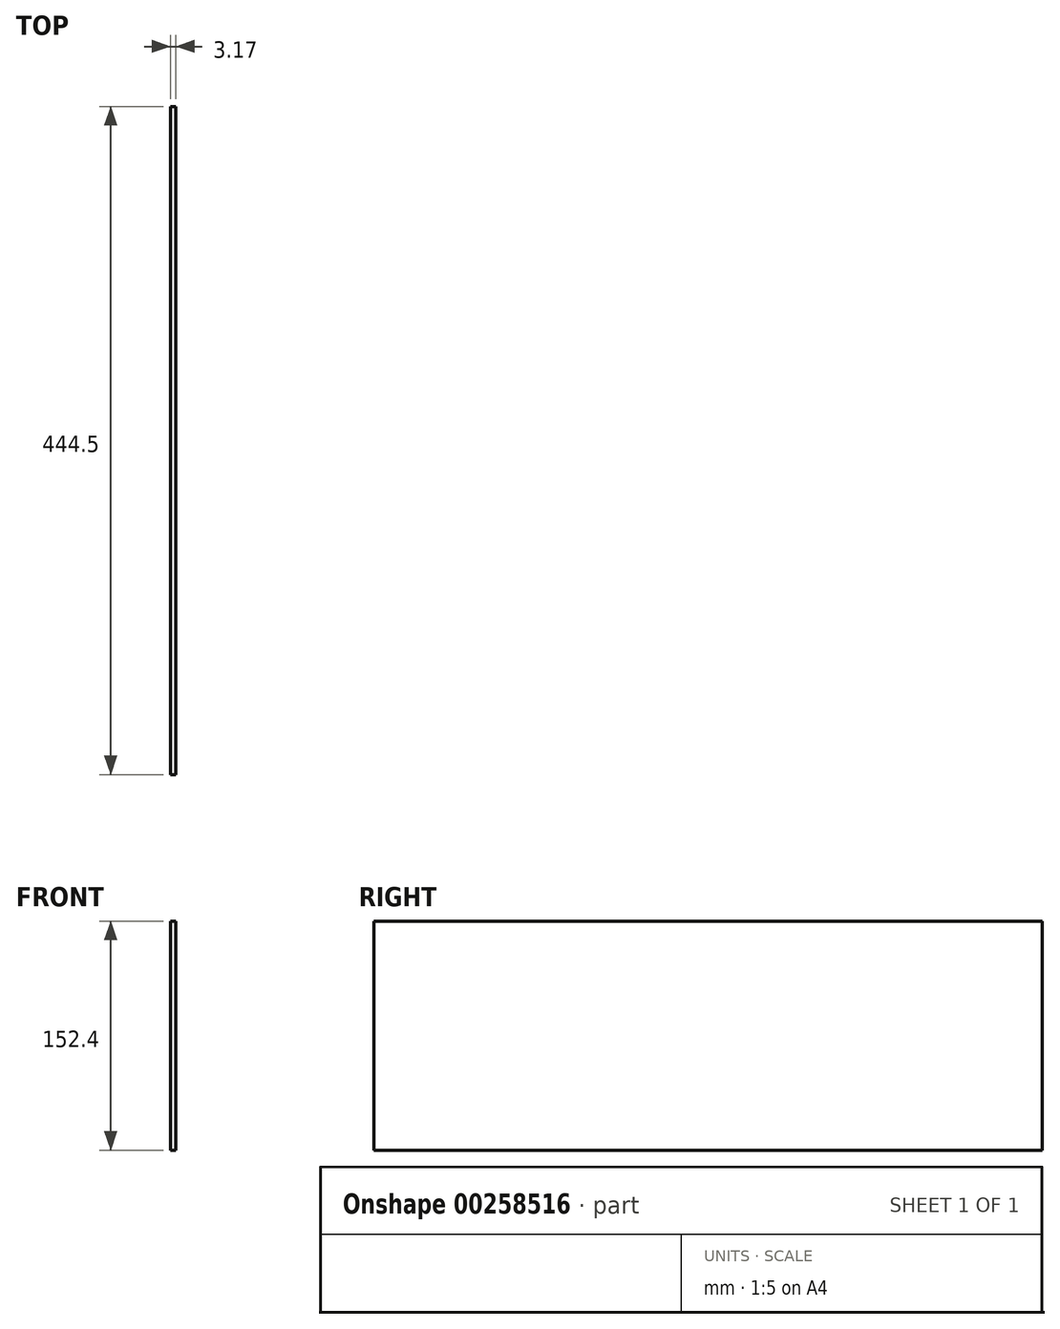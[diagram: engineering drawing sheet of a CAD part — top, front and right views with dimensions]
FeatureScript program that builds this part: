
annotation { "Feature Type Name" : "Feature", "Feature Type Description" : "" }
export const myFeature = defineFeature(function(context is Context, id is Id, definition is map)
    precondition{}
    {
        {
            var Q0;
            Q0=qCreatedBy(makeId("Right.planeOp"),FACE);
            var sketch = newSketch(context, id + "F0", { "sketchPlane" : qUnion([Q0])});
            skLineSegment(sketch, "E0.bottom", {"start": v(222.25, 76.2) * mm, "end": v(-222.25, 76.2) * mm});
            skLineSegment(sketch, "E0.top", {"start": v(222.25, -76.2) * mm, "end": v(-222.25, -76.2) * mm});
            skLineSegment(sketch, "E0.left", {"start": v(222.25, 76.2) * mm, "end": v(222.25, -76.2) * mm});
            skLineSegment(sketch, "E0.right", {"start": v(-222.25, 76.2) * mm, "end": v(-222.25, -76.2) * mm});
            skPoint(sketch, "E0.middle", {"position": v(0, 0) * mm});
            skSolve(sketch);
        }
        {
            var Q0;
            Q0 = qSketchRegion(id + "F0", true);
            extrude(context, id + "F1", {"entities" : qUnion([Q0]), "depth" : 3.17 * mm});
        }
    });
